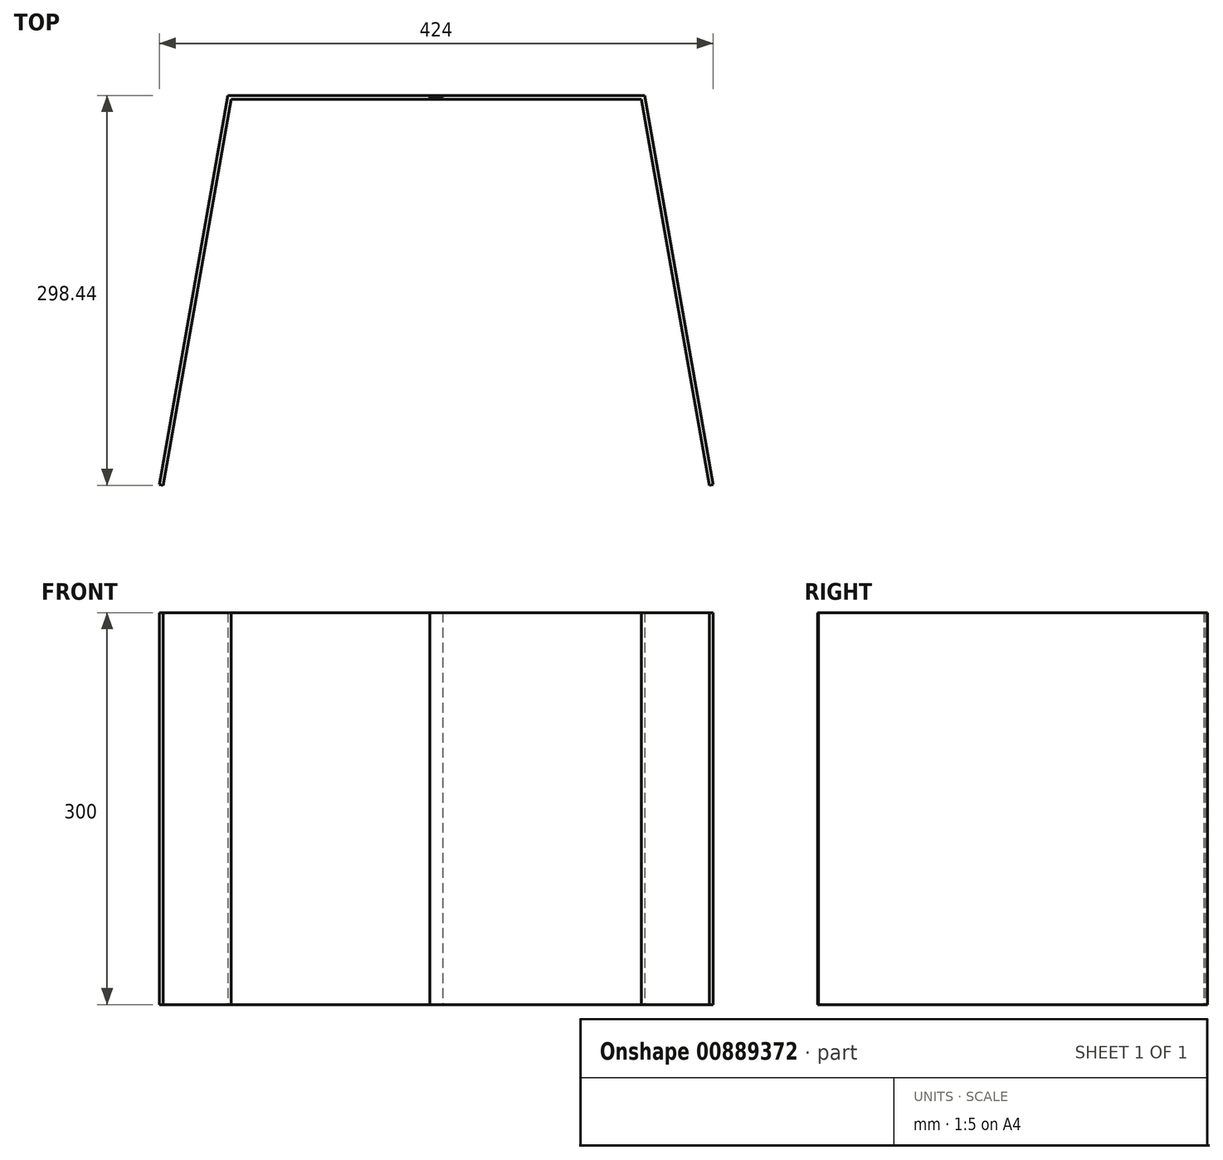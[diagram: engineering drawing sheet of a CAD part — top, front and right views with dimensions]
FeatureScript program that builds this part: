
annotation { "Feature Type Name" : "Feature", "Feature Type Description" : "" }
export const myFeature = defineFeature(function(context is Context, id is Id, definition is map)
    precondition{}
    {
        {
            var Q0;
            Q0=qCreatedBy(makeId("Top.planeOp"),FACE);
            var sketch = newSketch(context, id + "F0", { "sketchPlane" : qUnion([Q0])});
            skLineSegment(sketch, "E0.bottom", {"start": v(-160, 1.5) * mm, "end": v(160, 1.5) * mm});
            skLineSegment(sketch, "E0.top", {"start": v(-160, -1.5) * mm, "end": v(160, -1.5) * mm});
            skLineSegment(sketch, "E0.left", {"start": v(-160, 1.5) * mm, "end": v(-160, -1.5) * mm, "construction": true});
            skLineSegment(sketch, "E0.right", {"start": v(160, 1.5) * mm, "end": v(160, -1.5) * mm, "construction": true});
            skPoint(sketch, "E1", {"position": v(0, -1.5) * mm});
            skPoint(sketch, "E2", {"position": v(160, 0) * mm});
            skLineSegment(sketch, "E3", {"start": v(0, 1.5) * mm, "end": v(0, -1.5) * mm});
            skLineSegment(sketch, "E4", {"start": v(-160, 1.5) * mm, "end": v(-142.99, -1.5) * mm, "construction": true});
            skLineSegment(sketch, "E5", {"start": v(-156.95, -1.5) * mm, "end": v(-209.05, -296.94) * mm});
            skLineSegment(sketch, "E6", {"start": v(-209.05, -296.94) * mm, "end": v(-212, -296.42) * mm});
            skLineSegment(sketch, "E7", {"start": v(-212, -296.42) * mm, "end": v(-160, -1.5) * mm});
            skLineSegment(sketch, "E8", {"start": v(-160, -1.5) * mm, "end": v(-159.47, 1.5) * mm});
            skLineSegment(sketch, "E9", {"start": v(-5, 0) * mm, "end": v(5, 0) * mm});
            skLineSegment(sketch, "E10", {"start": v(-5, 0) * mm, "end": v(-5, -1.5) * mm});
            skLineSegment(sketch, "E11", {"start": v(5, 0) * mm, "end": v(5, 1.5) * mm});
            skLineSegment(sketch, "E12", {"start": v(0, -67.28) * mm, "end": v(0, 0) * mm, "construction": true});
            skLineSegment(sketch, "E13.MirrorCS", {"start": v(160, -1.5) * mm, "end": v(159.47, 1.5) * mm});
            skLineSegment(sketch, "E14.MirrorCS", {"start": v(156.95, -1.5) * mm, "end": v(209.05, -296.94) * mm});
            skLineSegment(sketch, "E15.MirrorCS", {"start": v(209.05, -296.94) * mm, "end": v(212, -296.42) * mm});
            skLineSegment(sketch, "E16.MirrorCS", {"start": v(212, -296.42) * mm, "end": v(160, -1.5) * mm});
            skSolve(sketch);
        }
        {
            var Q0;
            {var subQ2=sQuery(id+"F0.wireOp",EDGE,"E5");Q0=makeQuery(id+"F0.imprint","IMPRINT",FACE,{"disambiguationData":[TD([[makeQuery(id+"F0.imprint","IMPRINT",EDGE,{"derivedFrom":subQ2}),-1.0]])]});}
            var Q1;
            {var subQ8=sQuery(id+"F0.wireOp",EDGE,"E8");Q1=makeQuery(id+"F0.imprint","IMPRINT",FACE,{"disambiguationData":[TD([[makeQuery(id+"F0.imprint","IMPRINT",EDGE,{"derivedFrom":subQ8}),-1.0]])]});}
            var Q2;
            {var subQ3=sQuery(id+"F0.wireOp",EDGE,"E11");Q2=makeQuery(id+"F0.imprint","IMPRINT",FACE,{"disambiguationData":[TD([[makeQuery(id+"F0.imprint","IMPRINT",EDGE,{"derivedFrom":subQ3}),1.0]])]});}
            extrude(context, id + "F1", {"entities" : qUnion([Q0, Q1, Q2]), "depth" : 300 * mm, "offsetDistance" : 25 * mm});
        }
        {
            var Q0;
            {var subQ6=sQuery(id+"F0.wireOp",EDGE,"E11");Q0=makeQuery(id+"F0.imprint","IMPRINT",FACE,{"disambiguationData":[TD([[makeQuery(id+"F0.imprint","IMPRINT",EDGE,{"derivedFrom":subQ6}),-1.0]])]});}
            var Q1;
            {var subQ3=sQuery(id+"F0.wireOp",EDGE,"E10");Q1=makeQuery(id+"F0.imprint","IMPRINT",FACE,{"disambiguationData":[TD([[makeQuery(id+"F0.imprint","IMPRINT",EDGE,{"derivedFrom":subQ3}),1.0]])]});}
            var Q2;
            {var subQ2=sQuery(id+"F0.wireOp",EDGE,"E14.MirrorCS");Q2=makeQuery(id+"F0.imprint","IMPRINT",FACE,{"disambiguationData":[TD([[makeQuery(id+"F0.imprint","IMPRINT",EDGE,{"derivedFrom":subQ2}),1.0]])]});}
            extrude(context, id + "F2", {"entities" : qUnion([Q0, Q1, Q2]), "depth" : 300 * mm, "offsetDistance" : 25 * mm});
        }
    });
